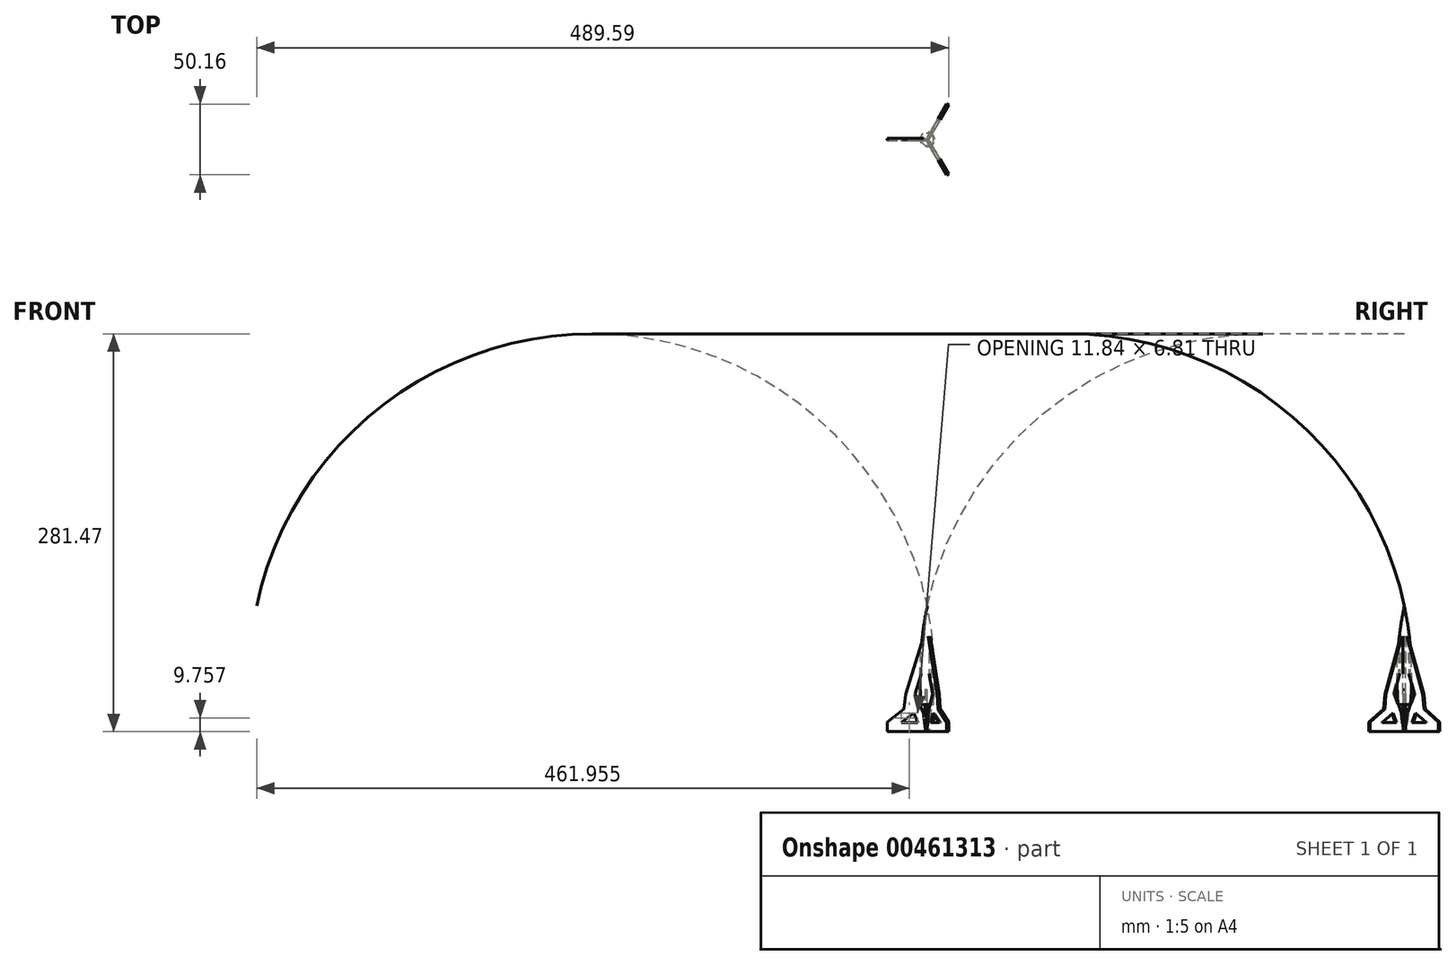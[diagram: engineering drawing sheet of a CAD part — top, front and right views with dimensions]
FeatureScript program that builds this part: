
annotation { "Feature Type Name" : "Feature", "Feature Type Description" : "" }
export const myFeature = defineFeature(function(context is Context, id is Id, definition is map)
    precondition{}
    {
        {
            var Q0;
            Q0=qCreatedBy(makeId("Front.planeOp"),FACE);
            var sketch = newSketch(context, id + "F0", { "sketchPlane" : qUnion([Q0])});
            skLineSegment(sketch, "E0", {"start": v(0, 0) * mm, "end": v(0, 63.5) * mm});
            skLineSegment(sketch, "E1", {"start": v(0, 0) * mm, "end": v(0, 25.4) * mm});
            skLineSegment(sketch, "E2", {"start": v(0, 25.4) * mm, "end": v(4.67, 25.4) * mm});
            skLineSegment(sketch, "E3", {"start": v(0, 0) * mm, "end": v(3.18, 0) * mm});
            skLineSegment(sketch, "E4", {"start": v(0, 0) * mm, "end": v(19.05, 0) * mm});
            skLineSegment(sketch, "E5", {"start": v(19.05, 0) * mm, "end": v(19.05, 6.35) * mm});
            skLineSegment(sketch, "E6", {"start": v(0, 0) * mm, "end": v(2.04, 0) * mm});
            skLineSegment(sketch, "E7", {"start": v(0, 0) * mm, "end": v(0, 19.05) * mm});
            skLineSegment(sketch, "E8", {"start": v(0, 19.05) * mm, "end": v(4.45, 19.05) * mm});
            skLineSegment(sketch, "E9", {"start": v(0, 63.5) * mm, "end": v(0, 88.9) * mm});
            skArc(sketch, "E10", {"start": v(2.04, 0) * mm, "mid": v(5.13, 44.54) * mm, "end": v(0, 88.9) * mm});
            skLineSegment(sketch, "E11", {"start": v(16.47, 26.4) * mm, "end": v(3.53, 67.33) * mm});
            skLineSegment(sketch, "E12.0", {"start": v(9.7, 26.76) * mm, "end": v(5.19, 41.04) * mm});
            skLineSegment(sketch, "E13", {"start": v(12.61, 17.56) * mm, "end": v(7.71, 6.35) * mm});
            skLineSegment(sketch, "E14.0", {"start": v(9.7, 26.76) * mm, "end": v(3.84, 13.34) * mm});
            skLineSegment(sketch, "E15", {"start": v(3.84, 13.34) * mm, "end": v(3.59, 12.76) * mm});
            skLineSegment(sketch, "E16", {"start": v(3.59, 12.76) * mm, "end": v(3.52, 12.61) * mm});
            skLineSegment(sketch, "E17", {"start": v(16.47, 26.4) * mm, "end": v(24.82, 0) * mm});
            skLineSegment(sketch, "E18", {"start": v(24.82, 0) * mm, "end": v(4.94, 0) * mm});
            skLineSegment(sketch, "E19.0", {"start": v(16.15, 6.35) * mm, "end": v(7.71, 6.35) * mm});
            skLineSegment(sketch, "E19.1", {"start": v(12.61, 17.56) * mm, "end": v(16.15, 6.35) * mm});
            skArc(sketch, "E20.MirrorCS", {"start": v(-2.04, 0) * mm, "mid": v(-5.13, 44.54) * mm, "end": v(0, 88.9) * mm});
            skLineSegment(sketch, "E21.MirrorCS", {"start": v(-16.47, 26.4) * mm, "end": v(-3.53, 67.33) * mm});
            skLineSegment(sketch, "E22.MirrorCS", {"start": v(-9.7, 26.76) * mm, "end": v(-5.19, 41.04) * mm});
            skLineSegment(sketch, "E23.MirrorCS", {"start": v(-9.7, 26.76) * mm, "end": v(-3.84, 13.34) * mm});
            skLineSegment(sketch, "E24", {"start": v(-16.47, 26.4) * mm, "end": v(-17.49, 15.95) * mm});
            skLineSegment(sketch, "E25", {"start": v(-29.45, 6.75) * mm, "end": v(-29.45, 0) * mm});
            skLineSegment(sketch, "E26", {"start": v(-29.45, 0) * mm, "end": v(-2.04, 0) * mm});
            skLineSegment(sketch, "E27", {"start": v(-29.45, 6.75) * mm, "end": v(-17.49, 15.95) * mm});
            skLineSegment(sketch, "E28.0", {"start": v(-19.56, 6.35) * mm, "end": v(-10.7, 13.16) * mm});
            skLineSegment(sketch, "E28.1", {"start": v(-19.56, 6.35) * mm, "end": v(-2.04, 6.35) * mm});
            skPoint(sketch, "E29.orphan", {"position": v(-9.7, 26.76) * mm});
            skLineSegment(sketch, "E30", {"start": v(-9.7, 26.76) * mm, "end": v(-10.7, 13.16) * mm});
            skLineSegment(sketch, "E31.0", {"start": v(-10.7, 13.16) * mm, "end": v(-7.71, 6.35) * mm});
            skPoint(sketch, "E32.orphan", {"position": v(-3.84, 13.34) * mm});
            skLineSegment(sketch, "E33", {"start": v(-3.84, 13.34) * mm, "end": v(-3.54, 12.66) * mm});
            skPoint(sketch, "E34", {"position": v(-3.54, 12.66) * mm});
            skSolve(sketch);
        }
        {
            var Q0;
            {var subQ0=sQuery(id+"F0.wireOp",EDGE,"E0");Q0=makeQuery(id+"F0.imprint","IMPRINT",FACE,{"disambiguationData":[TD([[makeQuery(id+"F0.imprint","IMPRINT",EDGE,{"derivedFrom":subQ0}),-1.0]])]});}
            var Q1;
            {var subQ0=sQuery(id+"F0.wireOp",EDGE,"E1");Q1=makeQuery(id+"F0.imprint","IMPRINT",FACE,{"disambiguationData":[TD([[makeQuery(id+"F0.imprint","IMPRINT",EDGE,{"derivedFrom":subQ0}),-1.0]])]});}
            var Q2;
            Q2=makeQuery(id+"F0.imprint","IMPRINT",FACE,{"disambiguationData":[TD([[makeQuery(id+"F0.imprint","IMPRINT",EDGE,{"derivedFrom":sQuery(id+"F0.wireOp",EDGE,"E6")}),1.0]])]});
            var Q3;
            Q3=sQuery(id+"F0.wireOp",EDGE,"E7");
            revolve(context, id + "F1", {"entities" : qUnion([Q0, Q1, Q2]), "axis" : qUnion([Q3]), "revolveType" : RevolveType.FULL});
        }
        {
            var Q0;
            {var subQ4=sQuery(id+"F0.wireOp",EDGE,"E5");Q0=makeQuery(id+"F0.imprint","IMPRINT",FACE,{"disambiguationData":[TD([[makeQuery(id+"F0.imprint","IMPRINT",EDGE,{"derivedFrom":subQ4}),1.0]])]});}
            var Q1;
            {var subQ3=sQuery(id+"F0.wireOp",EDGE,"nT6RCVWs-UBkZ-0Hko-ysXy-ktpMFyBmOWMN");Q1=makeQuery(id+"F0.imprint","IMPRINT",FACE,{"disambiguationData":[TD([[makeQuery(id+"F0.imprint","IMPRINT",EDGE,{"derivedFrom":subQ3}),-1.0]])]});}
            var Q2;
            {var subQ7=sQuery(id+"F0.wireOp",EDGE,"E21.MirrorCS");Q2=makeQuery(id+"F0.imprint","IMPRINT",FACE,{"disambiguationData":[TD([[makeQuery(id+"F0.imprint","IMPRINT",EDGE,{"derivedFrom":subQ7}),-1.0]])]});}
            var Q3;
            {var subQ4=sQuery(id+"F0.wireOp",EDGE,"E23.MirrorCS");Q3=makeQuery(id+"F0.imprint","IMPRINT",FACE,{"disambiguationData":[TD([[makeQuery(id+"F0.imprint","IMPRINT",EDGE,{"derivedFrom":subQ4}),-1.0]])]});}
            extrude(context, id + "F2", {"entities" : qUnion([Q0, Q1, Q2, Q3]), "depth" : 0.89 * mm, "hasSecondDirection" : true, "secondDirectionOppositeDirection" : true, "secondDirectionDepth" : 0.89 * mm});
        }
        {
            var Q0;
            Q0=qCreatedBy(makeId("Top.planeOp"),FACE);
            var sketch = newSketch(context, id + "F3", { "sketchPlane" : qUnion([Q0])});
            skLineSegment(sketch, "E35", {"start": v(18.99, 0) * mm, "end": v(16.06, 6.66) * mm});
            skLineSegment(sketch, "E36", {"start": v(16.06, 6.66) * mm, "end": v(16.86, 7.01) * mm});
            skLineSegment(sketch, "E37", {"start": v(16.86, 7.01) * mm, "end": v(19.94, 0) * mm});
            skLineSegment(sketch, "E38", {"start": v(19.94, 0) * mm, "end": v(18.99, 0) * mm});
            skSolve(sketch);
        }
        {
            var Q0;
            Q0=qCreatedBy(makeId("Front.planeOp"),FACE);
            var sketch = newSketch(context, id + "F4", { "sketchPlane" : qUnion([Q0])});
            skLineSegment(sketch, "E39", {"start": v(0, 0) * mm, "end": v(0, 29.62) * mm});
            skLineSegment(sketch, "E40", {"start": v(0, 29.62) * mm, "end": v(-1.6, 29.62) * mm});
            skLineSegment(sketch, "E41", {"start": v(-1.6, 29.62) * mm, "end": v(-1.6, 0) * mm});
            skLineSegment(sketch, "E42", {"start": v(-1.6, 0) * mm, "end": v(0, 0) * mm});
            skSolve(sketch);
        }
        {
            var Q0;
            Q0=qSketchRegion(id+"F4",true);
            extrude(context, id + "F5", {"entities" : qUnion([Q0]), "depth" : 0.64 * mm});
        }
        {
            var Q0;
            Q0=makeQuery(id+"F2.opExtrude","SWEPT_BODY",BODY,{"disambiguationData":[OSD([sQuery(id+"F0.wireOp",EDGE,"E20.MirrorCS"),sQuery(id+"F0.wireOp",EDGE,"nT6RCVWs-UBkZ-0Hko-ysXy-ktpMFyBmOWMN"),sQuery(id+"F0.wireOp",EDGE,"oj1umrom-CwAz-DrqZ-iLGO-JDcrMx9Gn4y1"),sQuery(id+"F0.wireOp",EDGE,"cvmb7Ydq-cFWo-3DIN-3vk7-AgfzJjxBXpjo"),sQuery(id+"F0.wireOp",EDGE,"iiXuzMc4-C4GC-oAon-SKex-5jeGhQqnXeoi"),sQuery(id+"F0.wireOp",EDGE,"1d65bcdd-b8af-4602-8e8b-9e1d1ba82597.0"),sQuery(id+"F0.wireOp",EDGE,"1d65bcdd-b8af-4602-8e8b-9e1d1ba82597.1"),sQuery(id+"F0.wireOp",EDGE,"1d65bcdd-b8af-4602-8e8b-9e1d1ba82597.2"),sQuery(id+"F0.wireOp",EDGE,"ZcZrK82t-RwEe-16NU-uMeW-Dd9Ma3mYJGpj"),sQuery(id+"F0.wireOp",EDGE,"06bda9d8-7904-47ba-bfa6-5a50b3d8344e.0"),sQuery(id+"F0.wireOp",EDGE,"6ddf1f63-d790-4f41-b818-1a6a03fafacd.trimOffspring")])]});
            transform(context, id + "F6", {"entities" : qUnion([Q0]), "transformType" : TransformType.TRANSLATION_3D, "dx" : 1 * mm, "dy" : 0 * mm, "dz" : 0 * mm, "makeCopy" : false});
        }
        {
            var Q0;
            Q0=makeQuery(id+"F2.opExtrude","SWEPT_BODY",BODY,{"disambiguationData":[OSD([sQuery(id+"F0.wireOp",EDGE,"E20.MirrorCS"),sQuery(id+"F0.wireOp",EDGE,"nT6RCVWs-UBkZ-0Hko-ysXy-ktpMFyBmOWMN"),sQuery(id+"F0.wireOp",EDGE,"oj1umrom-CwAz-DrqZ-iLGO-JDcrMx9Gn4y1"),sQuery(id+"F0.wireOp",EDGE,"cvmb7Ydq-cFWo-3DIN-3vk7-AgfzJjxBXpjo"),sQuery(id+"F0.wireOp",EDGE,"iiXuzMc4-C4GC-oAon-SKex-5jeGhQqnXeoi"),sQuery(id+"F0.wireOp",EDGE,"1d65bcdd-b8af-4602-8e8b-9e1d1ba82597.0"),sQuery(id+"F0.wireOp",EDGE,"1d65bcdd-b8af-4602-8e8b-9e1d1ba82597.1"),sQuery(id+"F0.wireOp",EDGE,"1d65bcdd-b8af-4602-8e8b-9e1d1ba82597.2"),sQuery(id+"F0.wireOp",EDGE,"ZcZrK82t-RwEe-16NU-uMeW-Dd9Ma3mYJGpj"),sQuery(id+"F0.wireOp",EDGE,"06bda9d8-7904-47ba-bfa6-5a50b3d8344e.0"),sQuery(id+"F0.wireOp",EDGE,"6ddf1f63-d790-4f41-b818-1a6a03fafacd.trimOffspring")])]});
            var Q1;
            Q1=sQuery(id+"F0.wireOp",EDGE,"E7");
            circularPattern(context, id + "F7", {"entities" : qUnion([Q0]), "axis" : qUnion([Q1]), "angle" : 360 * degree, "instanceCount" : 3, "equalSpace" : true});
        }
    });
